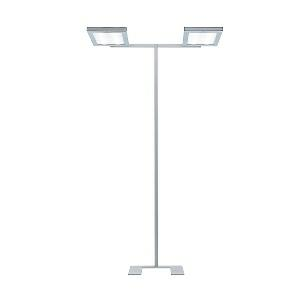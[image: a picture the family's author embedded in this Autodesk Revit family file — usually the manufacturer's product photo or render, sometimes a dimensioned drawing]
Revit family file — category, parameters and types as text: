
# Revit family: lavigo_-_dps_30000_840_r_g2a_-_twin-u_00808535_6c3a
name_source: partatom
category: Lighting Fixtures
units: mm (PartAtom-declared; Revit-internal decimal feet)

## family parameters
Cut with Voids When Loaded = No
Host = Face
Light Source = No
Part Type = Normal
Room Calculation Point = No
Round Connector Dimension = Use Diameter
Shared = No

## types (1)
- LAVIGO - DPS 30000/840/R/G2A - TWIN-U (1 x LED, 15250 lm, 4000K)
    Apparent Load = 210 VA
    Approval mark = CE
    CIE Flux Codes = 60 87 97 11 100
    Color Rendering = 80-89
    Color Temperature = 4000K
    Default Elevation = 1800 mm
    Description = DPS 30000/840/R/G2A|Free-standing luminaire|light source: LED|work equipment: Electronic ballast|connected load: 220-240 V, 50/60 Hz|Power consumption: approx. 210 W|standby: approx. 0,50|power factor: approx. 0,966|luminous flux: 30500 lm|luminous efficacy: 145 lm/W|light distribution: Direct/indirect|direct ratio: approx. 12 %|colour temperature: Cold white, ca. 4000 K|color rendering index (CRI): >= 80|chromaticity tolerance:  3 SDCM|technology: Presence and daylight sensor control (PIR)|operation: Multi-function switch, Touch-LED|luminaire body|material: Steel/plastic|surface: Painted|colour: Silver metallic|lamp cover: Acrylic (PMMA), Satine|tubular section|material: Steel tube|surface: Painted|Form: Tubular section upright|colour of tubular section: Silver metallic|luminaire base|Form: C-form flat|weight (net): approx. 27.6 kg|mains lead: 3.00 m Mains plug CEE 7/VII|Fastening: Floor standing base|decorative contrast side parts: Flint grey|glare control: Prism aperture|luminance(L65): <= 3000 cd/m|unified glare rating(4H 8H): <=  16|special features: Luminaire head detachable, Asymmetric radiation, Direct light component with edge light and light-guide technology for homogenous light exit, Flicker-free, Integrated light and presence sensor PIR, Retrofittable with TALK module, Separated, direct and indirect light individually adjustable|
    Height = 36 mm
    Lamp = 1 x LED
    Lamp Light Flux = 15250 lm
    Lamp count = 1
    Length = 675 mm
    Luminous efficacy = 145 lm/W
    Manufacturer = Waldmann
    ModVariant = No
    Model = 00808535
    Mounting Place = Floor
    Mounting Type = Freestanding
    Number of Poles = 1
    OnlyDefault = Yes
    Power Factor = 1
    Product Name = LAVIGO - DPS 30000/840/R/G2A - TWIN-U
    Product group = Free standing luminaire
    ProductGroupID = 13
    Protection Class = Protection class I
    Protection Degree = IP 20
    RLX_Detail_Level = 1
    RLX_Emergency_Light_Flux = 0 lm
    RLX_Emergency_Type = 0
    RLX_Emergency_Type_DB = No
    RlxData = <blob elided: 41961 chars, md5=ca0960dd>
    Socket = socket
    Standby Power = 0 W
    System Light Flux = 30500 lm
    System Power = 210 W
    Type Comments = Product without accessories
    Type Image = 121714000-00642982.jpg
    URL = http://relux.com
    VarID = ---
    Voltage = 0 V
    Weight = 0.00 kg
    Width = 350 mm

## geometry (parser evidence)
native form markers: Blend x4, Sweep x18
no freeform markers — native parametric forms only
